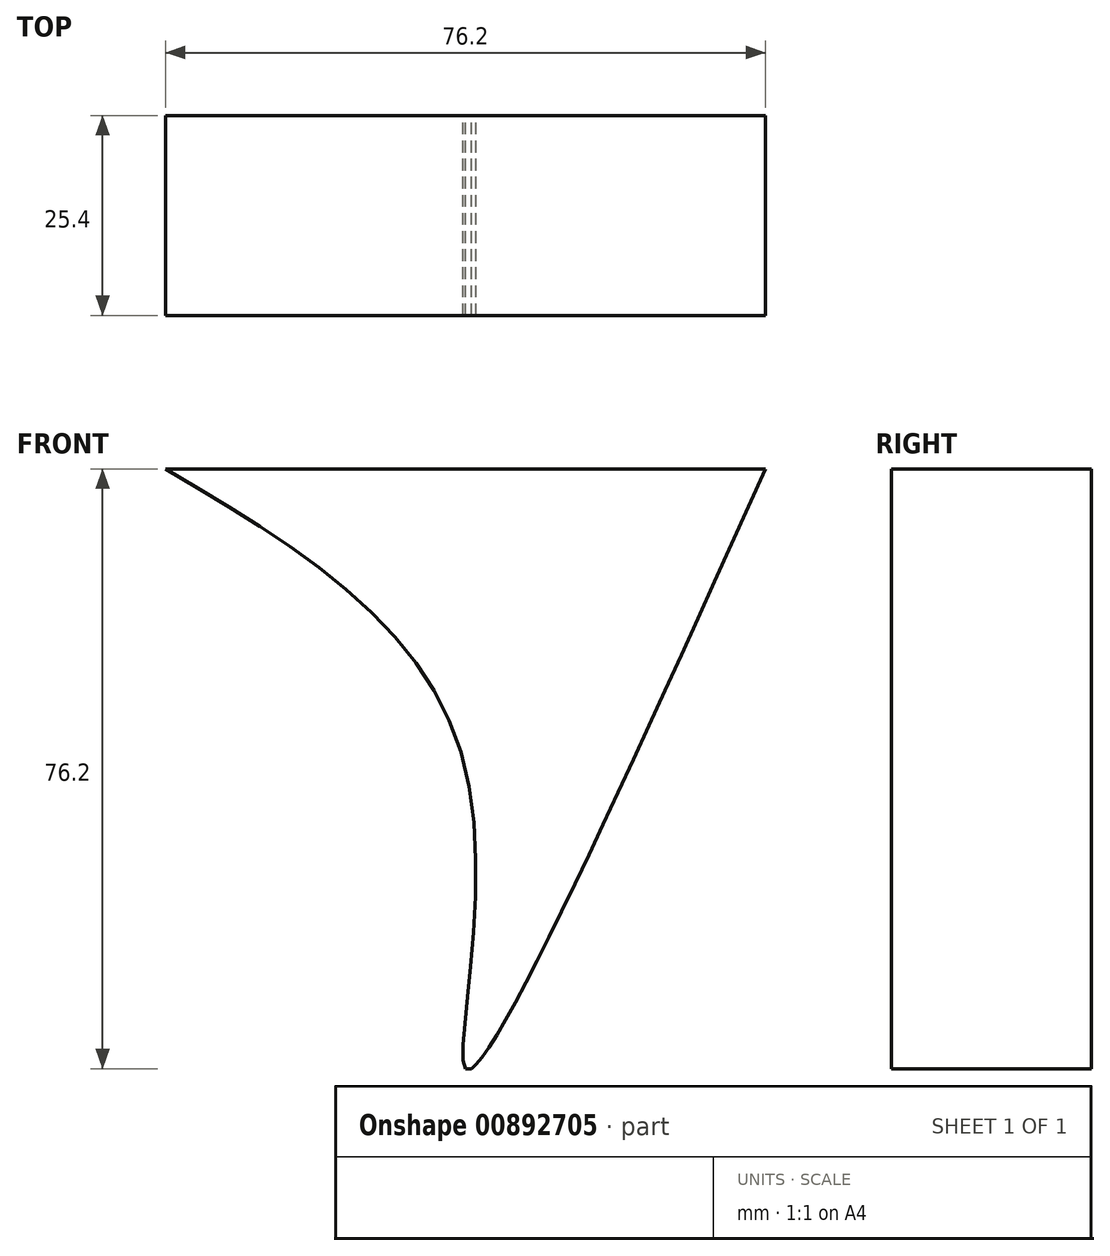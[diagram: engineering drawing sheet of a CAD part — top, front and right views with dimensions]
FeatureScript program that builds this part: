
annotation { "Feature Type Name" : "Feature", "Feature Type Description" : "" }
export const myFeature = defineFeature(function(context is Context, id is Id, definition is map)
    precondition{}
    {
        {
            var Q0;
            Q0=qCreatedBy(makeId("Front.planeOp"),FACE);
            var sketch = newSketch(context, id + "F0", { "sketchPlane" : qUnion([Q0])});
            skLineSegment(sketch, "E0.bottom", {"start": v(38.1, -38.1) * mm, "end": v(-38.1, -38.1) * mm});
            skLineSegment(sketch, "E0.top", {"start": v(38.1, 38.1) * mm, "end": v(-38.1, 38.1) * mm});
            skLineSegment(sketch, "E0.left", {"start": v(38.1, -38.1) * mm, "end": v(38.1, 38.1) * mm});
            skLineSegment(sketch, "E0.right", {"start": v(-38.1, -38.1) * mm, "end": v(-38.1, 38.1) * mm});
            skPoint(sketch, "E0.middle", {"position": v(0, 0) * mm});
            skFitSpline(sketch, "E1", {"points": [v(-38.1, 38.1) * mm, v(0, 0) * mm, v(0, -38.1) * mm, v(38.1, 38.1) * mm], "startDerivative": vector(157, -92.97) * mm, "endDerivative": vector(131.82, 292.4) * mm});
            skSolve(sketch);
        }
        {
            var Q0;
            {var subQ4=sQuery(id+"F0.wireOp",EDGE,"E0.top");Q0=makeQuery(id+"F0.imprint","IMPRINT",FACE,{"disambiguationData":[TD([[makeQuery(id+"F0.imprint","IMPRINT",EDGE,{"derivedFrom":subQ4}),1.0]])]});}
            extrude(context, id + "F1", {"entities" : qUnion([Q0]), "depth" : 25.4 * mm, "offsetDistance" : 25.4 * mm});
        }
    });
